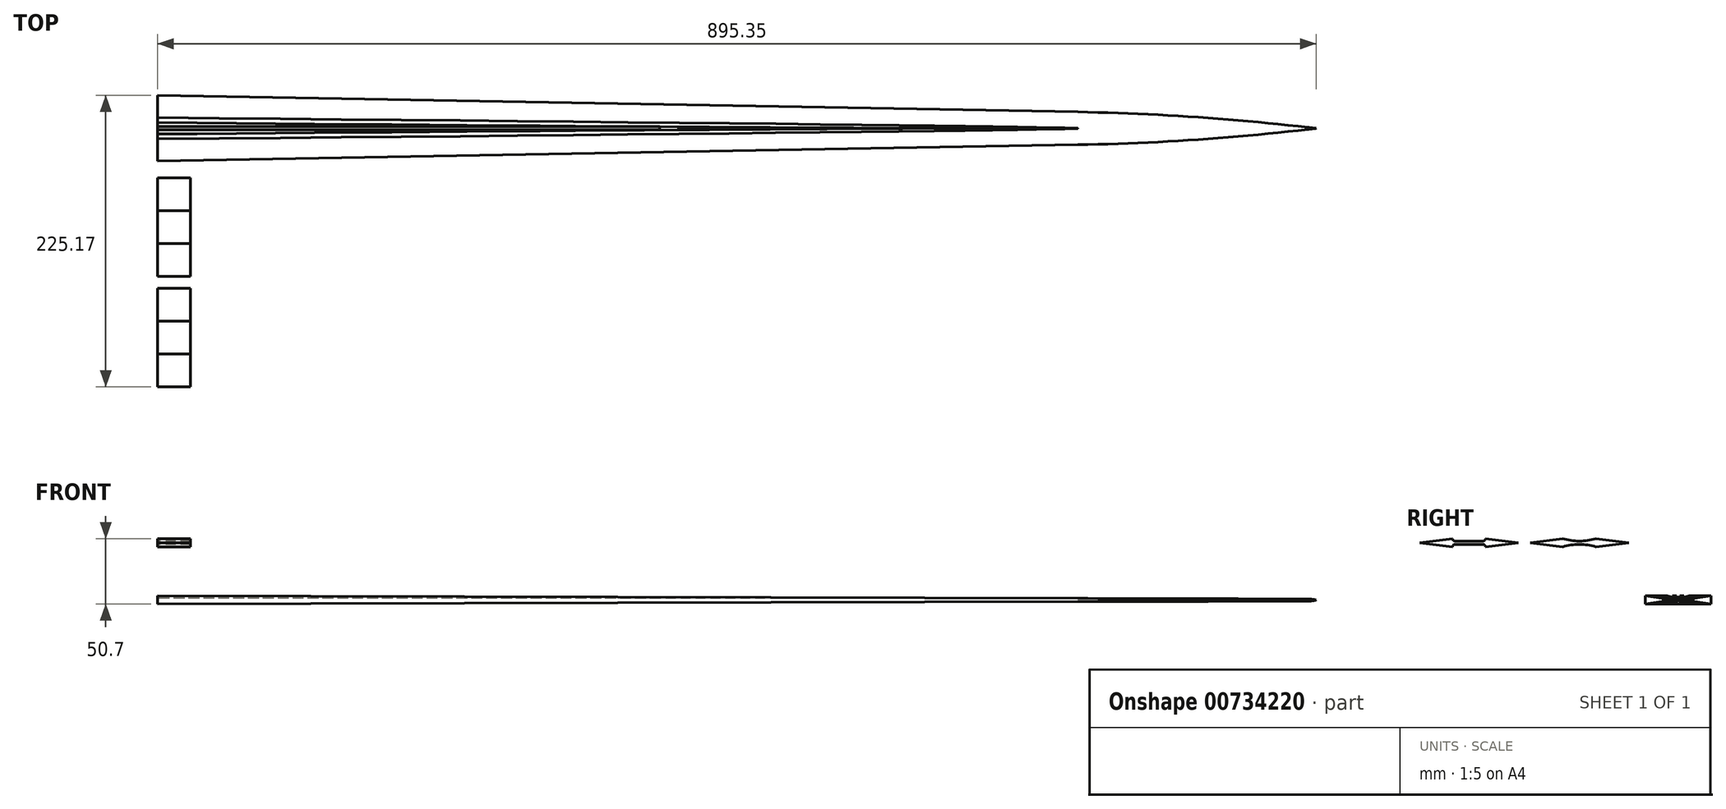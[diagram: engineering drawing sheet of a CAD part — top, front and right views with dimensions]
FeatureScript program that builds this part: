
annotation { "Feature Type Name" : "Feature", "Feature Type Description" : "" }
export const myFeature = defineFeature(function(context is Context, id is Id, definition is map)
    precondition{}
    {
        {
            var Q0;
            Q0=qCreatedBy(makeId("Front.planeOp"),FACE);
            var sketch = newSketch(context, id + "F0", { "sketchPlane" : qUnion([Q0])});
            skLineSegment(sketch, "E0", {"start": v(0, 3.18) * mm, "end": v(889, 0.8) * mm});
            skLineSegment(sketch, "E1", {"start": v(889, 0.8) * mm, "end": v(889, -0.8) * mm, "construction": true});
            skLineSegment(sketch, "E2", {"start": v(889, -0.8) * mm, "end": v(0, -3.18) * mm});
            skLineSegment(sketch, "E3", {"start": v(0, -3.18) * mm, "end": v(0, 3.18) * mm});
            skLineSegment(sketch, "E4", {"start": v(0, 0) * mm, "end": v(889, 0) * mm, "construction": true});
            skArc(sketch, "E5", {"start": v(895.35, 0) * mm, "mid": v(892.2, 0.6) * mm, "end": v(889, 0.8) * mm});
            skArc(sketch, "E6", {"start": v(889, -0.8) * mm, "mid": v(892.2, -0.6) * mm, "end": v(895.35, 0) * mm});
            skSolve(sketch);
        }
        {
            var Q0;
            Q0 = qSketchRegion(id + "F0", true);
            extrude(context, id + "F1", {"entities" : qUnion([Q0]), "depth" : 25.4 * mm, "offsetDistance" : 25.4 * mm, "hasSecondDirection" : true, "secondDirectionOppositeDirection" : true, "secondDirectionDepth" : 25.4 * mm});
        }
        {
            var Q0;
            Q0=qCreatedBy(makeId("Top.planeOp"),FACE);
            var sketch = newSketch(context, id + "F2", { "sketchPlane" : qUnion([Q0])});
            skLineSegment(sketch, "E7", {"start": v(0, 25.4) * mm, "end": v(711.2, 12.7) * mm});
            skLineSegment(sketch, "E8", {"start": v(711.2, 12.7) * mm, "end": v(711.2, -12.7) * mm, "construction": true});
            skLineSegment(sketch, "E9", {"start": v(711.2, -12.7) * mm, "end": v(0, -25.4) * mm});
            skLineSegment(sketch, "E10", {"start": v(0, -25.4) * mm, "end": v(0, 25.4) * mm, "construction": true});
            skLineSegment(sketch, "E11", {"start": v(0, 0) * mm, "end": v(711.2, 0) * mm, "construction": true});
            skArc(sketch, "E12", {"start": v(895.35, 0) * mm, "mid": v(803.44, 8.7) * mm, "end": v(711.2, 12.7) * mm});
            skArc(sketch, "E13", {"start": v(711.2, -12.7) * mm, "mid": v(803.44, -8.7) * mm, "end": v(895.35, 0) * mm});
            skLineSegment(sketch, "E14", {"start": v(0, 25.4) * mm, "end": v(3.16, 202.31) * mm});
            skLineSegment(sketch, "E15", {"start": v(3.16, 202.31) * mm, "end": v(947.7, 202.31) * mm});
            skLineSegment(sketch, "E16", {"start": v(947.7, 202.31) * mm, "end": v(947.7, -301.82) * mm});
            skLineSegment(sketch, "E17", {"start": v(947.7, -301.82) * mm, "end": v(0, -301.82) * mm});
            skLineSegment(sketch, "E18", {"start": v(0, -301.82) * mm, "end": v(0, -25.4) * mm});
            skSolve(sketch);
        }
        {
            var Q0;
            Q0 = qSketchRegion(id + "F2", true);
            extrude(context, id + "F3", {"entities" : qUnion([Q0]), "operationType" : NewBodyOperationType.REMOVE, "oppositeDirection" : true, "depth" : 25.4 * mm, "offsetDistance" : 25.4 * mm, "hasSecondDirection" : true, "secondDirectionOppositeDirection" : false, "secondDirectionDepth" : 25.4 * mm});
        }
        {
            var Q0;
            Q0=qCreatedBy(makeId("Right.planeOp"),FACE);
            var sketch = newSketch(context, id + "F4", { "sketchPlane" : qUnion([Q0])});
            skLineSegment(sketch, "E19.bottom", {"start": v(6.35, 20.32) * mm, "end": v(3.8, 20.32) * mm});
            skLineSegment(sketch, "E19.top", {"start": v(6.35, 1.27) * mm, "end": v(3.81, 1.27) * mm});
            skLineSegment(sketch, "E19.left", {"start": v(6.35, 20.32) * mm, "end": v(6.35, 1.27) * mm});
            skLineSegment(sketch, "E19.right", {"start": v(3.8, 20.32) * mm, "end": v(3.81, 1.27) * mm});
            skLineSegment(sketch, "E20.bottom", {"start": v(-6.35, 1.27) * mm, "end": v(6.35, 1.27) * mm, "construction": true});
            skLineSegment(sketch, "E20.top", {"start": v(-6.35, -1.27) * mm, "end": v(6.35, -1.27) * mm, "construction": true});
            skLineSegment(sketch, "E20.left", {"start": v(-6.35, 1.27) * mm, "end": v(-6.35, -1.27) * mm, "construction": true});
            skLineSegment(sketch, "E20.right", {"start": v(6.35, 1.27) * mm, "end": v(6.35, -1.27) * mm, "construction": true});
            skPoint(sketch, "E20.middle", {"position": v(0, 0) * mm});
            skLineSegment(sketch, "E21.bottom", {"start": v(3.8, 20.32) * mm, "end": v(1.27, 20.32) * mm});
            skLineSegment(sketch, "E21.top", {"start": v(3.81, 1.27) * mm, "end": v(1.27, 1.27) * mm});
            skLineSegment(sketch, "E21.right", {"start": v(1.27, 20.32) * mm, "end": v(1.27, 1.27) * mm});
            skLineSegment(sketch, "E22.bottom", {"start": v(1.27, 20.32) * mm, "end": v(-1.27, 20.32) * mm});
            skLineSegment(sketch, "E22.top", {"start": v(1.27, 1.27) * mm, "end": v(-1.27, 1.27) * mm});
            skLineSegment(sketch, "E22.right", {"start": v(-1.27, 20.32) * mm, "end": v(-1.27, 1.27) * mm});
            skLineSegment(sketch, "E23.bottom", {"start": v(-3.81, 20.32) * mm, "end": v(-6.35, 20.32) * mm});
            skLineSegment(sketch, "E23.top", {"start": v(-3.8, 1.27) * mm, "end": v(-6.35, 1.27) * mm});
            skLineSegment(sketch, "E23.left", {"start": v(-3.8, 20.32) * mm, "end": v(-3.81, 1.27) * mm});
            skLineSegment(sketch, "E23.right", {"start": v(-6.35, 20.32) * mm, "end": v(-6.35, 1.27) * mm});
            skLineSegment(sketch, "E24.bottom", {"start": v(-1.27, 20.32) * mm, "end": v(-3.81, 20.32) * mm});
            skLineSegment(sketch, "E24.top", {"start": v(-1.27, 1.27) * mm, "end": v(-3.8, 1.27) * mm});
            skLineSegment(sketch, "E24.right", {"start": v(-3.81, 20.32) * mm, "end": v(-3.8, 1.27) * mm});
            skSolve(sketch);
        }
        {
            var Q0;
            Q0=makeQuery(id+"F3.boolean.opBoolean","MERGE",EDGE,{"derivedFrom":[makeQuery(id+"F1.opExtrude","CAP_EDGE",EDGE,{"disambiguationData":[OSD([sQuery(id+"F0.wireOp",EDGE,"E3")])],"isStart":false}),makeQuery(id+"F3.opExtrude","SWEPT_EDGE",EDGE,{"disambiguationData":[OSD([sQuery(id+"F2.wireOp",EDGE,"E9"),sQuery(id+"F2.wireOp",EDGE,"E18")])]})]});
            cPlane(context, id + "F5", {"entities" : qUnion([Q0]), "cplaneType" : CPlaneType.LINE_ANGLE, "offset" : 25.4 * mm, "angle" : .511556 * degree, "width" : 152.4 * mm, "height" : 152.4 * mm});
        }
        {
            var Q0;
            Q0=qCreatedBy(id+"F5.planeOp",FACE);
            var sketch = newSketch(context, id + "F6", { "sketchPlane" : qUnion([Q0])});
            skLineSegment(sketch, "E25.0.3", {"start": v(6.35, 3.18) * mm, "end": v(25.4, 3.18) * mm, "construction": true});
            skLineSegment(sketch, "E25.0.4", {"start": v(25.4, 3.18) * mm, "end": v(25.4, -3.18) * mm, "construction": true});
            skLineSegment(sketch, "E25.0.5", {"start": v(25.4, -3.18) * mm, "end": v(-25.4, -3.18) * mm, "construction": true});
            skLineSegment(sketch, "E25.0.6", {"start": v(-25.4, -3.18) * mm, "end": v(-25.4, 3.17) * mm, "construction": true});
            skLineSegment(sketch, "E25.0.7", {"start": v(-25.4, 3.18) * mm, "end": v(-6.35, 3.18) * mm, "construction": true});
            skCircle(sketch, "E26", {"center": v(-6.35, 3.18) * mm, "radius": 1.9 * mm});
            skSolve(sketch);
        }
        {
            var Q0;
            Q0 = qSketchRegion(id + "F6", true);
            extrude(context, id + "F7", {"entities" : qUnion([Q0]), "operationType" : NewBodyOperationType.REMOVE, "depth" : 762 * mm, "offsetDistance" : 25.4 * mm});
        }
        {
            var Q0;
            Q0=sQuery(id+"F6.wireOp",EDGE,"E25.0.4");
            cPlane(context, id + "F8", {"entities" : qUnion([Q0]), "cplaneType" : CPlaneType.LINE_ANGLE, "offset" : 25.4 * mm, "angle" : .511556 * degree, "width" : 152.4 * mm, "height" : 152.4 * mm});
        }
        {
            var Q0;
            Q0=qCreatedBy(id+"F8.planeOp",FACE);
            var sketch = newSketch(context, id + "F9", { "sketchPlane" : qUnion([Q0])});
            skCircle(sketch, "E27", {"center": v(-6.34, 3.18) * mm, "radius": 1.9 * mm});
            skSolve(sketch);
        }
        {
            var Q0;
            Q0 = qSketchRegion(id + "F9", true);
            extrude(context, id + "F10", {"entities" : qUnion([Q0]), "operationType" : NewBodyOperationType.REMOVE, "oppositeDirection" : true, "depth" : 762 * mm, "offsetDistance" : 25.4 * mm});
        }
        {
            var Q0;
            Q0=makeQuery(id+"F4.imprint","IMPRINT",FACE,{"disambiguationData":[TD([[makeQuery(id+"F4.imprint","IMPRINT",EDGE,{"derivedFrom":sQuery(id+"F4.wireOp",EDGE,"E22.bottom")}),1.0]])]});
            extrude(context, id + "F11", {"entities" : qUnion([Q0]), "operationType" : NewBodyOperationType.REMOVE, "depth" : 387.96 * mm, "offsetDistance" : 25.4 * mm});
        }
        {
            var Q0;
            Q0=qCreatedBy(makeId("Right.planeOp"),FACE);
            var sketch = newSketch(context, id + "F12", { "sketchPlane" : qUnion([Q0])});
            skLineSegment(sketch, "E28", {"start": v(-123.57, 44.36) * mm, "end": v(-199.77, 44.36) * mm, "construction": true});
            skLineSegment(sketch, "E29", {"start": v(-199.77, 44.36) * mm, "end": v(-174.37, 47.53) * mm});
            skLineSegment(sketch, "E30", {"start": v(-172.46, 45.63) * mm, "end": v(-150.87, 45.63) * mm});
            skLineSegment(sketch, "E31", {"start": v(-123.57, 44.36) * mm, "end": v(-148.97, 47.53) * mm});
            skLineSegment(sketch, "E32", {"start": v(-114.47, 44.36) * mm, "end": v(-89.07, 47.53) * mm});
            skLineSegment(sketch, "E33", {"start": v(-63.67, 47.53) * mm, "end": v(-38.27, 44.36) * mm});
            skLineSegment(sketch, "E34", {"start": v(-38.27, 44.36) * mm, "end": v(-114.47, 44.36) * mm, "construction": true});
            skArc(sketch, "E35", {"start": v(-89.07, 47.53) * mm, "mid": v(-76.37, 45.63) * mm, "end": v(-63.67, 47.53) * mm});
            skArc(sketch, "E36", {"start": v(-174.37, 47.53) * mm, "mid": v(-173.81, 46.18) * mm, "end": v(-172.46, 45.63) * mm});
            skArc(sketch, "E37", {"start": v(-150.87, 45.63) * mm, "mid": v(-149.53, 46.18) * mm, "end": v(-148.97, 47.53) * mm});
            skLineSegment(sketch, "E38", {"start": v(-89.07, 47.53) * mm, "end": v(-63.67, 47.53) * mm, "construction": true});
            skLineSegment(sketch, "E39.MirrorCS", {"start": v(-199.77, 44.36) * mm, "end": v(-174.37, 41.18) * mm});
            skLineSegment(sketch, "E40.MirrorCS", {"start": v(-172.46, 43.09) * mm, "end": v(-150.87, 43.09) * mm});
            skLineSegment(sketch, "E41.MirrorCS", {"start": v(-123.57, 44.36) * mm, "end": v(-148.97, 41.18) * mm});
            skArc(sketch, "E42.MirrorCS", {"start": v(-150.87, 43.09) * mm, "mid": v(-149.53, 42.53) * mm, "end": v(-148.97, 41.18) * mm});
            skArc(sketch, "E43.MirrorCS", {"start": v(-174.37, 41.18) * mm, "mid": v(-173.81, 42.53) * mm, "end": v(-172.46, 43.09) * mm});
            skLineSegment(sketch, "E44.MirrorCS", {"start": v(-114.47, 44.36) * mm, "end": v(-89.07, 41.18) * mm});
            skArc(sketch, "E45.MirrorCS", {"start": v(-89.07, 41.18) * mm, "mid": v(-76.37, 43.09) * mm, "end": v(-63.67, 41.18) * mm});
            skLineSegment(sketch, "E46.MirrorCS", {"start": v(-89.07, 41.18) * mm, "end": v(-63.67, 41.18) * mm, "construction": true});
            skLineSegment(sketch, "E47.MirrorCS", {"start": v(-63.67, 41.18) * mm, "end": v(-38.27, 44.36) * mm});
            skLineSegment(sketch, "E48", {"start": v(-174.37, 47.53) * mm, "end": v(-148.97, 47.53) * mm, "construction": true});
            skSolve(sketch);
        }
        {
            var Q0;
            Q0 = qSketchRegion(id + "F12", true);
            extrude(context, id + "F13", {"entities" : qUnion([Q0]), "depth" : 25.4 * mm, "offsetDistance" : 25.4 * mm});
        }
    });
